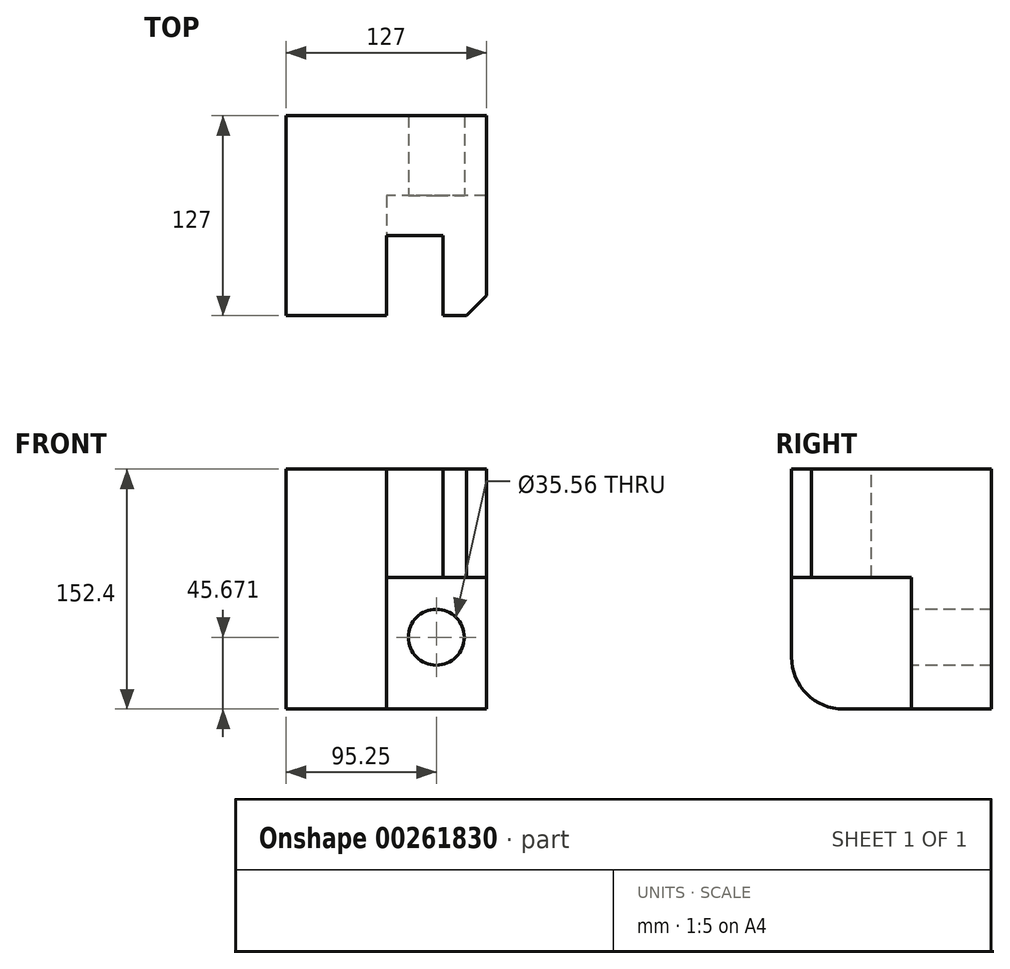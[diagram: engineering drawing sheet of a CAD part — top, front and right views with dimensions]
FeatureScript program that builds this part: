
annotation { "Feature Type Name" : "Feature", "Feature Type Description" : "" }
export const myFeature = defineFeature(function(context is Context, id is Id, definition is map)
    precondition{}
    {
        {
            var Q0;
            Q0=qCreatedBy(makeId("Front.planeOp"),FACE);
            var sketch = newSketch(context, id + "F0", { "sketchPlane" : qUnion([Q0])});
            skLineSegment(sketch, "E0.bottom", {"start": v(63.5, -76.2) * mm, "end": v(-63.5, -76.2) * mm});
            skLineSegment(sketch, "E0.top", {"start": v(63.5, 76.2) * mm, "end": v(-63.5, 76.2) * mm});
            skLineSegment(sketch, "E0.left", {"start": v(63.5, -76.2) * mm, "end": v(63.5, 76.2) * mm});
            skLineSegment(sketch, "E0.right", {"start": v(-63.5, -76.2) * mm, "end": v(-63.5, 76.2) * mm});
            skPoint(sketch, "E0.middle", {"position": v(0, 0) * mm});
            skSolve(sketch);
        }
        {
            var Q0;
            Q0=makeQuery(id+"F0.imprint","IMPRINT",FACE,{"disambiguationData":[TD([[makeQuery(id+"F0.imprint","IMPRINT",EDGE,{"derivedFrom":sQuery(id+"F0.wireOp",EDGE,"E0.bottom")}),-1.0]])]});
            extrude(context, id + "F1", {"entities" : qUnion([Q0]), "depth" : 127 * mm});
        }
        {
            var Q0;
            Q0=makeQuery(id+"F1.opExtrude","CAP_FACE",FACE,{"disambiguationData":[OSD([sQuery(id+"F0.wireOp",EDGE,"E0.bottom"),sQuery(id+"F0.wireOp",EDGE,"E0.top"),sQuery(id+"F0.wireOp",EDGE,"E0.left"),sQuery(id+"F0.wireOp",EDGE,"E0.right")])],"isStart":false});
            var sketch = newSketch(context, id + "F2", { "sketchPlane" : qUnion([Q0])});
            skLineSegment(sketch, "E1.bottom", {"start": v(63.5, -76.2) * mm, "end": v(0, -76.2) * mm});
            skLineSegment(sketch, "E1.top", {"start": v(63.5, 7.57) * mm, "end": v(0, 7.57) * mm});
            skLineSegment(sketch, "E1.left", {"start": v(63.5, -76.2) * mm, "end": v(63.5, 7.57) * mm});
            skLineSegment(sketch, "E1.right", {"start": v(0, -76.2) * mm, "end": v(0, 7.57) * mm});
            skSolve(sketch);
        }
        {
            var Q0;
            Q0=makeQuery(id+"F2.imprint","IMPRINT",FACE,{"disambiguationData":[TD([[makeQuery(id+"F2.imprint","IMPRINT",EDGE,{"derivedFrom":sQuery(id+"F2.wireOp",EDGE,"E1.bottom")}),-1.0]])]});
            extrude(context, id + "F3", {"entities" : qUnion([Q0]), "operationType" : NewBodyOperationType.REMOVE, "oppositeDirection" : true, "depth" : 76.2 * mm});
        }
        {
            var Q0;
            Q0=makeQuery(id+"F3.boolean.opBoolean","COPY",FACE,{"derivedFrom":makeQuery(id+"F3.opExtrude","CAP_FACE",FACE,{"disambiguationData":[OSD([sQuery(id+"F2.wireOp",EDGE,"E1.bottom"),sQuery(id+"F2.wireOp",EDGE,"E1.top"),sQuery(id+"F2.wireOp",EDGE,"E1.left"),sQuery(id+"F2.wireOp",EDGE,"E1.right")])],"isStart":false})});
            var sketch = newSketch(context, id + "F4", { "sketchPlane" : qUnion([Q0])});
            skCircle(sketch, "E2", {"center": v(31.75, -30.53) * mm, "radius": 17.78 * mm});
            skSolve(sketch);
        }
        {
            var Q0;
            Q0=makeQuery(id+"F4.imprint","IMPRINT",FACE,{"disambiguationData":[TD([[makeQuery(id+"F4.imprint","IMPRINT",EDGE,{"derivedFrom":sQuery(id+"F4.wireOp",EDGE,"E2")}),1.0]])]});
            extrude(context, id + "F5", {"entities" : qUnion([Q0]), "operationType" : NewBodyOperationType.REMOVE, "endBound" : BoundingType.UP_TO_NEXT, "oppositeDirection" : true, "depth" : 50.8 * mm});
        }
        {
            var Q0;
            Q0=makeQuery(id+"F1.opExtrude","CAP_FACE",FACE,{"disambiguationData":[OSD([sQuery(id+"F0.wireOp",EDGE,"E0.bottom"),sQuery(id+"F0.wireOp",EDGE,"E0.top"),sQuery(id+"F0.wireOp",EDGE,"E0.left"),sQuery(id+"F0.wireOp",EDGE,"E0.right")])],"isStart":false});
            var sketch = newSketch(context, id + "F6", { "sketchPlane" : qUnion([Q0])});
            skLineSegment(sketch, "E3.bottom", {"start": v(0, 7.57) * mm, "end": v(35.94, 7.57) * mm});
            skLineSegment(sketch, "E3.top", {"start": v(0, 76.2) * mm, "end": v(35.94, 76.2) * mm});
            skLineSegment(sketch, "E3.left", {"start": v(0, 7.57) * mm, "end": v(0, 76.2) * mm});
            skLineSegment(sketch, "E3.right", {"start": v(35.94, 7.57) * mm, "end": v(35.94, 76.2) * mm});
            skSolve(sketch);
        }
        {
            var Q0;
            Q0=makeQuery(id+"F6.imprint","IMPRINT",FACE,{"disambiguationData":[TD([[makeQuery(id+"F6.imprint","IMPRINT",EDGE,{"derivedFrom":sQuery(id+"F6.wireOp",EDGE,"E3.bottom")}),-1.0]])]});
            extrude(context, id + "F7", {"entities" : qUnion([Q0]), "operationType" : NewBodyOperationType.REMOVE, "oppositeDirection" : true, "depth" : 50.8 * mm});
        }
        {
            var Q0;
            Q0=makeQuery(id+"F1.opExtrude","CAP_EDGE",EDGE,{"disambiguationData":[OSD([sQuery(id+"F0.wireOp",EDGE,"E0.bottom")])],"isStart":false});
            fillet(context, id + "F8", {"entities" : qUnion([Q0]), "radius" : 33.02 * mm, "tangentPropagation" : true, "allowEdgeOverflow" : false});
        }
        {
            var Q0;
            Q0=makeQuery(id+"F1.opExtrude","CAP_EDGE",EDGE,{"disambiguationData":[OSD([sQuery(id+"F0.wireOp",EDGE,"E0.left")])],"isStart":false});
            chamfer(context, id + "F9", {"entities" : qUnion([Q0]), "width" : 12.7 * mm, "tangentPropagation" : true});
        }
    });
